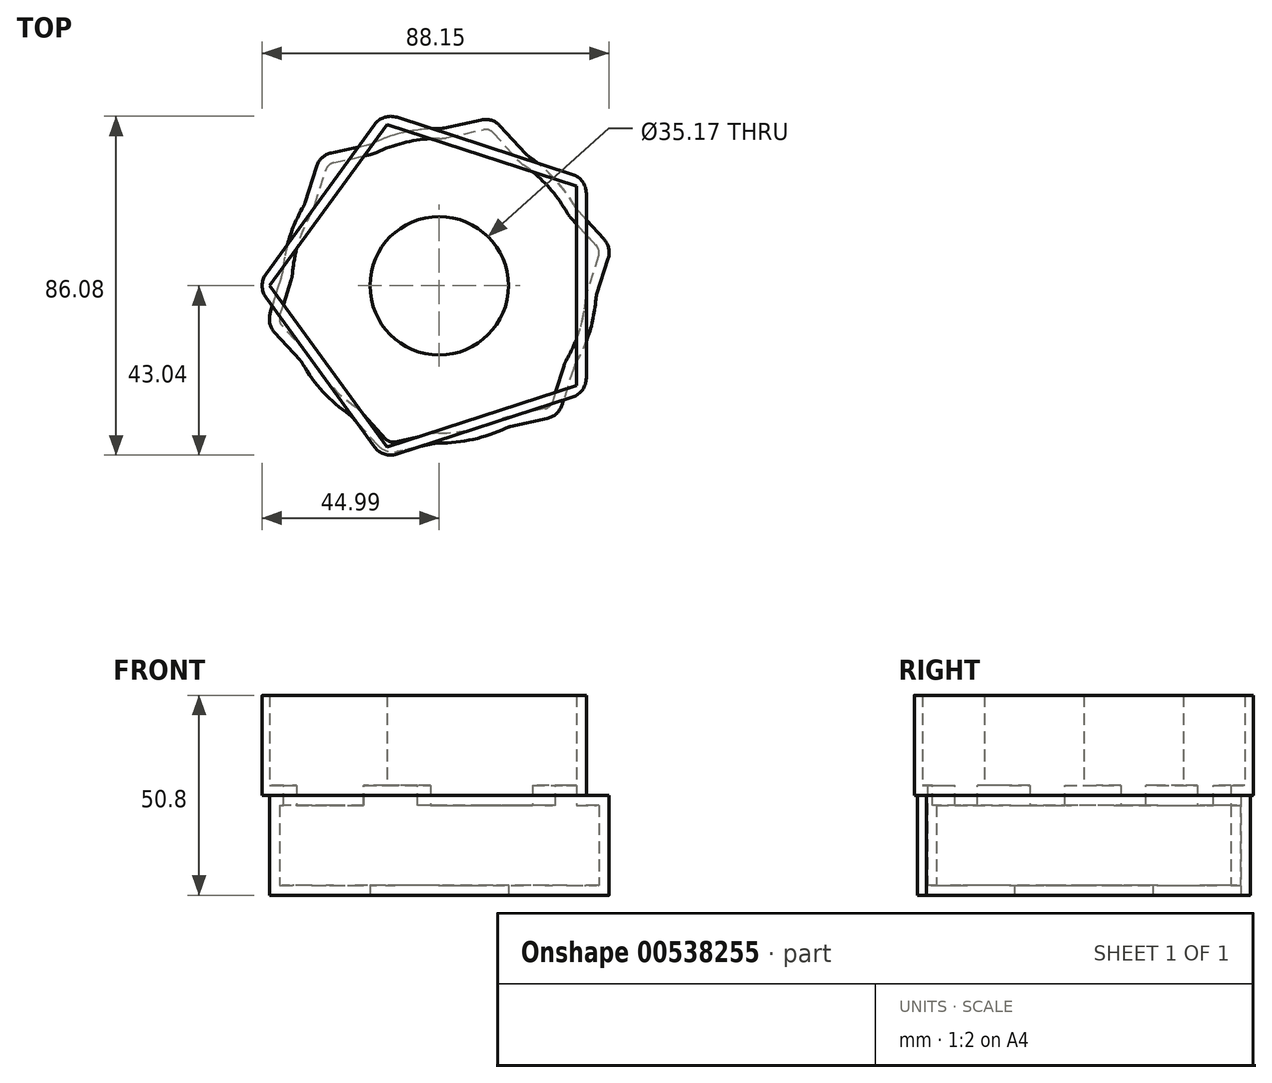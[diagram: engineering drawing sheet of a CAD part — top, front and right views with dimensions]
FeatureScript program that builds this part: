
annotation { "Feature Type Name" : "Feature", "Feature Type Description" : "" }
export const myFeature = defineFeature(function(context is Context, id is Id, definition is map)
    precondition{}
    {
        {
            var Q0;
            Q0=qCreatedBy(makeId("Top.planeOp"),FACE);
            var sketch = newSketch(context, id + "F0", { "sketchPlane" : qUnion([Q0])});
            skCircle(sketch, "E0", {"center": v(0, 0) * mm, "radius": 39.95 * mm});
            skSolve(sketch);
        }
        {
            var Q0;
            Q0 = qSketchRegion(id + "F0", true);
            extrude(context, id + "F1", {"entities" : qUnion([Q0]), "depth" : 25.4 * mm, "offsetDistance" : 25.4 * mm});
        }
        {
            var Q0;
            Q0=qCreatedBy(makeId("Top.planeOp"),FACE);
            var sketch = newSketch(context, id + "F2", { "sketchPlane" : qUnion([Q0])});
            skCircle(sketch, "E1.cCircle", {"center": v(0, 0) * mm, "radius": 44.86 * mm, "construction": true});
            skLineSegment(sketch, "E1.0", {"start": v(-43.8, -9.68) * mm, "end": v(-30.29, 33.1) * mm});
            skLineSegment(sketch, "E1.1", {"start": v(-30.29, 33.1) * mm, "end": v(13.52, 42.78) * mm});
            skLineSegment(sketch, "E1.2", {"start": v(13.52, 42.78) * mm, "end": v(43.8, 9.68) * mm});
            skLineSegment(sketch, "E1.3", {"start": v(43.8, 9.68) * mm, "end": v(30.29, -33.1) * mm});
            skLineSegment(sketch, "E1.4", {"start": v(30.29, -33.1) * mm, "end": v(-13.52, -42.78) * mm});
            skLineSegment(sketch, "E1.5", {"start": v(-13.52, -42.78) * mm, "end": v(-43.8, -9.68) * mm});
            skSolve(sketch);
        }
        {
            var Q0;
            Q0 = qSketchRegion(id + "F2", true);
            extrude(context, id + "F3", {"entities" : qUnion([Q0]), "operationType" : NewBodyOperationType.ADD, "depth" : 25.4 * mm, "offsetDistance" : 25.4 * mm});
        }
        {
            var Q0;
            Q0=makeQuery(id+"F3.opExtrude","SWEPT_EDGE",EDGE,{"disambiguationData":[OSD([sQuery(id+"F2.wireOp",EDGE,"E1.0"),sQuery(id+"F2.wireOp",EDGE,"E1.5")])]});
            var Q1;
            Q1=makeQuery(id+"F3.boolean.opBoolean","INTERSECT",EDGE,{"disambiguationData":[OD(0.0)],"derivedFrom":[makeQuery(id+"F1.opExtrude","SWEPT_FACE",FACE,{"disambiguationData":[OSD([sQuery(id+"F0.wireOp",EDGE,"E0")])]}),makeQuery(id+"F3.opExtrude","SWEPT_FACE",FACE,{"disambiguationData":[OSD([sQuery(id+"F2.wireOp",EDGE,"E1.0")])]})]});
            var Q2;
            Q2=makeQuery(id+"F3.boolean.opBoolean","INTERSECT",EDGE,{"disambiguationData":[OD(1.0)],"derivedFrom":[makeQuery(id+"F1.opExtrude","SWEPT_FACE",FACE,{"disambiguationData":[OSD([sQuery(id+"F0.wireOp",EDGE,"E0")])]}),makeQuery(id+"F3.opExtrude","SWEPT_FACE",FACE,{"disambiguationData":[OSD([sQuery(id+"F2.wireOp",EDGE,"E1.0")])]})]});
            var Q3;
            Q3=makeQuery(id+"F3.boolean.opBoolean","INTERSECT",EDGE,{"disambiguationData":[OD(0.0)],"derivedFrom":[makeQuery(id+"F1.opExtrude","SWEPT_FACE",FACE,{"disambiguationData":[OSD([sQuery(id+"F0.wireOp",EDGE,"E0")])]}),makeQuery(id+"F3.opExtrude","SWEPT_FACE",FACE,{"disambiguationData":[OSD([sQuery(id+"F2.wireOp",EDGE,"E1.5")])]})]});
            fillet(context, id + "F4", {"entities" : qUnion([Q0, Q1, Q2, Q3]), "radius" : 5.08 * mm, "tangentPropagation" : true, "allowEdgeOverflow" : false});
        }
        {
            var Q0;
            Q0=makeQuery(id+"F3.boolean.opBoolean","INTERSECT",EDGE,{"disambiguationData":[OD(1.0)],"derivedFrom":[makeQuery(id+"F1.opExtrude","SWEPT_FACE",FACE,{"disambiguationData":[OSD([sQuery(id+"F0.wireOp",EDGE,"E0")])]}),makeQuery(id+"F3.opExtrude","SWEPT_FACE",FACE,{"disambiguationData":[OSD([sQuery(id+"F2.wireOp",EDGE,"E1.5")])]})]});
            var Q1;
            Q1=makeQuery(id+"F3.opExtrude","SWEPT_EDGE",EDGE,{"disambiguationData":[OSD([sQuery(id+"F2.wireOp",EDGE,"E1.4"),sQuery(id+"F2.wireOp",EDGE,"E1.5")])]});
            var Q2;
            Q2=makeQuery(id+"F3.boolean.opBoolean","INTERSECT",EDGE,{"disambiguationData":[OD(1.0)],"derivedFrom":[makeQuery(id+"F1.opExtrude","SWEPT_FACE",FACE,{"disambiguationData":[OSD([sQuery(id+"F0.wireOp",EDGE,"E0")])]}),makeQuery(id+"F3.opExtrude","SWEPT_FACE",FACE,{"disambiguationData":[OSD([sQuery(id+"F2.wireOp",EDGE,"E1.4")])]})]});
            var Q3;
            Q3=makeQuery(id+"F3.boolean.opBoolean","INTERSECT",EDGE,{"disambiguationData":[OD(0.0)],"derivedFrom":[makeQuery(id+"F1.opExtrude","SWEPT_FACE",FACE,{"disambiguationData":[OSD([sQuery(id+"F0.wireOp",EDGE,"E0")])]}),makeQuery(id+"F3.opExtrude","SWEPT_FACE",FACE,{"disambiguationData":[OSD([sQuery(id+"F2.wireOp",EDGE,"E1.4")])]})]});
            var Q4;
            Q4=makeQuery(id+"F3.opExtrude","SWEPT_EDGE",EDGE,{"disambiguationData":[OSD([sQuery(id+"F2.wireOp",EDGE,"E1.3"),sQuery(id+"F2.wireOp",EDGE,"E1.4")])]});
            var Q5;
            Q5=makeQuery(id+"F3.boolean.opBoolean","INTERSECT",EDGE,{"disambiguationData":[OD(1.0)],"derivedFrom":[makeQuery(id+"F1.opExtrude","SWEPT_FACE",FACE,{"disambiguationData":[OSD([sQuery(id+"F0.wireOp",EDGE,"E0")])]}),makeQuery(id+"F3.opExtrude","SWEPT_FACE",FACE,{"disambiguationData":[OSD([sQuery(id+"F2.wireOp",EDGE,"E1.3")])]})]});
            var Q6;
            Q6=makeQuery(id+"F3.boolean.opBoolean","INTERSECT",EDGE,{"disambiguationData":[OD(0.0)],"derivedFrom":[makeQuery(id+"F1.opExtrude","SWEPT_FACE",FACE,{"disambiguationData":[OSD([sQuery(id+"F0.wireOp",EDGE,"E0")])]}),makeQuery(id+"F3.opExtrude","SWEPT_FACE",FACE,{"disambiguationData":[OSD([sQuery(id+"F2.wireOp",EDGE,"E1.3")])]})]});
            var Q7;
            Q7=makeQuery(id+"F3.opExtrude","SWEPT_EDGE",EDGE,{"disambiguationData":[OSD([sQuery(id+"F2.wireOp",EDGE,"E1.2"),sQuery(id+"F2.wireOp",EDGE,"E1.3")])]});
            var Q8;
            Q8=makeQuery(id+"F3.boolean.opBoolean","INTERSECT",EDGE,{"disambiguationData":[OD(1.0)],"derivedFrom":[makeQuery(id+"F1.opExtrude","SWEPT_FACE",FACE,{"disambiguationData":[OSD([sQuery(id+"F0.wireOp",EDGE,"E0")])]}),makeQuery(id+"F3.opExtrude","SWEPT_FACE",FACE,{"disambiguationData":[OSD([sQuery(id+"F2.wireOp",EDGE,"E1.2")])]})]});
            var Q9;
            Q9=makeQuery(id+"F3.boolean.opBoolean","INTERSECT",EDGE,{"disambiguationData":[OD(0.0)],"derivedFrom":[makeQuery(id+"F1.opExtrude","SWEPT_FACE",FACE,{"disambiguationData":[OSD([sQuery(id+"F0.wireOp",EDGE,"E0")])]}),makeQuery(id+"F3.opExtrude","SWEPT_FACE",FACE,{"disambiguationData":[OSD([sQuery(id+"F2.wireOp",EDGE,"E1.2")])]})]});
            var Q10;
            Q10=makeQuery(id+"F3.opExtrude","SWEPT_EDGE",EDGE,{"disambiguationData":[OSD([sQuery(id+"F2.wireOp",EDGE,"E1.1"),sQuery(id+"F2.wireOp",EDGE,"E1.2")])]});
            var Q11;
            Q11=makeQuery(id+"F3.boolean.opBoolean","INTERSECT",EDGE,{"disambiguationData":[OD(1.0)],"derivedFrom":[makeQuery(id+"F1.opExtrude","SWEPT_FACE",FACE,{"disambiguationData":[OSD([sQuery(id+"F0.wireOp",EDGE,"E0")])]}),makeQuery(id+"F3.opExtrude","SWEPT_FACE",FACE,{"disambiguationData":[OSD([sQuery(id+"F2.wireOp",EDGE,"E1.1")])]})]});
            var Q12;
            Q12=makeQuery(id+"F3.boolean.opBoolean","INTERSECT",EDGE,{"disambiguationData":[OD(0.0)],"derivedFrom":[makeQuery(id+"F1.opExtrude","SWEPT_FACE",FACE,{"disambiguationData":[OSD([sQuery(id+"F0.wireOp",EDGE,"E0")])]}),makeQuery(id+"F3.opExtrude","SWEPT_FACE",FACE,{"disambiguationData":[OSD([sQuery(id+"F2.wireOp",EDGE,"E1.1")])]})]});
            var Q13;
            Q13=makeQuery(id+"F3.opExtrude","SWEPT_EDGE",EDGE,{"disambiguationData":[OSD([sQuery(id+"F2.wireOp",EDGE,"E1.0"),sQuery(id+"F2.wireOp",EDGE,"E1.1")])]});
            var Q14;
            {var subQ4=sQuery(id+"F2.wireOp",EDGE,"E1.1");var subQ5=sQuery(id+"F2.wireOp",EDGE,"E1.0");var subQ6=sQuery(id+"F0.wireOp",EDGE,"E0");var subQ7=makeQuery(id+"F1.opExtrude","SWEPT_FACE",FACE,{"disambiguationData":[OSD([subQ6])]});var subQ8=makeQuery(id+"F3.opExtrude","SWEPT_FACE",FACE,{"disambiguationData":[OSD([subQ5])]});Q14=makeQuery(id+"F4.opFillet","BLEND_EDGE",EDGE,{"blendedFrom":[makeQuery(id+"F3.boolean.opBoolean","INTERSECT",EDGE,{"disambiguationData":[OD(1.0)],"derivedFrom":[subQ7,subQ8]}),makeQuery(id+"F3.boolean.opBoolean","SPLIT",FACE,{"disambiguationData":[TD([makeQuery(id+"F3.opExtrude","SWEPT_FACE",FACE,{"disambiguationData":[OSD([subQ4])]})])],"derivedFrom":subQ8})],"blendedInto":[makeQuery(id+"F3.boolean.opBoolean","SPLIT",FACE,{"disambiguationData":[TD([makeQuery(id+"F3.opExtrude","SWEPT_FACE",FACE,{"disambiguationData":[OSD([subQ4])]})])],"derivedFrom":subQ8})]});}
            var Q15;
            {var subQ0=sQuery(id+"F2.wireOp",EDGE,"E1.5");var subQ5=sQuery(id+"F2.wireOp",EDGE,"E1.0");var subQ6=sQuery(id+"F0.wireOp",EDGE,"E0");var subQ7=makeQuery(id+"F1.opExtrude","SWEPT_FACE",FACE,{"disambiguationData":[OSD([subQ6])]});var subQ8=makeQuery(id+"F3.opExtrude","SWEPT_FACE",FACE,{"disambiguationData":[OSD([subQ5])]});Q15=makeQuery(id+"F4.opFillet","BLEND_EDGE",EDGE,{"blendedFrom":[makeQuery(id+"F3.boolean.opBoolean","INTERSECT",EDGE,{"disambiguationData":[OD(0.0)],"derivedFrom":[subQ7,subQ8]}),makeQuery(id+"F3.boolean.opBoolean","SPLIT",FACE,{"disambiguationData":[TD([makeQuery(id+"F3.opExtrude","SWEPT_FACE",FACE,{"disambiguationData":[OSD([subQ0])]})])],"derivedFrom":subQ8})],"blendedInto":[makeQuery(id+"F3.boolean.opBoolean","SPLIT",FACE,{"disambiguationData":[TD([makeQuery(id+"F3.opExtrude","SWEPT_FACE",FACE,{"disambiguationData":[OSD([subQ0])]})])],"derivedFrom":subQ8})]});}
            var Q16;
            {var subQ0=sQuery(id+"F2.wireOp",EDGE,"E1.0");var subQ2=sQuery(id+"F2.wireOp",EDGE,"E1.5");Q16=makeQuery(id+"F4.opFillet","BLEND_EDGE",EDGE,{"blendedFrom":[makeQuery(id+"F3.opExtrude","SWEPT_EDGE",EDGE,{"disambiguationData":[OSD([subQ0,subQ2])]}),makeQuery(id+"F3.boolean.opBoolean","SPLIT",FACE,{"disambiguationData":[TD([makeQuery(id+"F3.opExtrude","SWEPT_FACE",FACE,{"disambiguationData":[OSD([subQ0])]})])],"derivedFrom":makeQuery(id+"F3.opExtrude","SWEPT_FACE",FACE,{"disambiguationData":[OSD([subQ2])]})})],"blendedInto":[makeQuery(id+"F3.boolean.opBoolean","SPLIT",FACE,{"disambiguationData":[TD([makeQuery(id+"F3.opExtrude","SWEPT_FACE",FACE,{"disambiguationData":[OSD([subQ0])]})])],"derivedFrom":makeQuery(id+"F3.opExtrude","SWEPT_FACE",FACE,{"disambiguationData":[OSD([subQ2])]})})]});}
            var Q17;
            {var subQ0=sQuery(id+"F2.wireOp",EDGE,"E1.5");var subQ5=sQuery(id+"F2.wireOp",EDGE,"E1.0");Q17=makeQuery(id+"F4.opFillet","BLEND_EDGE",EDGE,{"blendedFrom":[makeQuery(id+"F3.opExtrude","SWEPT_EDGE",EDGE,{"disambiguationData":[OSD([subQ5,subQ0])]}),makeQuery(id+"F3.boolean.opBoolean","SPLIT",FACE,{"disambiguationData":[TD([makeQuery(id+"F3.opExtrude","SWEPT_FACE",FACE,{"disambiguationData":[OSD([subQ0])]})])],"derivedFrom":makeQuery(id+"F3.opExtrude","SWEPT_FACE",FACE,{"disambiguationData":[OSD([subQ5])]})})],"blendedInto":[makeQuery(id+"F3.boolean.opBoolean","SPLIT",FACE,{"disambiguationData":[TD([makeQuery(id+"F3.opExtrude","SWEPT_FACE",FACE,{"disambiguationData":[OSD([subQ0])]})])],"derivedFrom":makeQuery(id+"F3.opExtrude","SWEPT_FACE",FACE,{"disambiguationData":[OSD([subQ5])]})})]});}
            fillet(context, id + "F5", {"entities" : qUnion([Q0, Q1, Q2, Q3, Q4, Q5, Q6, Q7, Q8, Q9, Q10, Q11, Q12, Q13, Q14, Q15, Q16, Q17]), "radius" : 5.08 * mm, "tangentPropagation" : true, "allowEdgeOverflow" : false});
        }
        {
            var Q0;
            Q0=makeQuery(id+"F3.boolean.opBoolean","MERGE",FACE,{"derivedFrom":[makeQuery(id+"F1.opExtrude","CAP_FACE",FACE,{"disambiguationData":[OSD([sQuery(id+"F0.wireOp",EDGE,"E0")])],"isStart":false}),makeQuery(id+"F3.opExtrude","CAP_FACE",FACE,{"disambiguationData":[OSD([sQuery(id+"F2.wireOp",EDGE,"E1.0"),sQuery(id+"F2.wireOp",EDGE,"E1.1"),sQuery(id+"F2.wireOp",EDGE,"E1.2"),sQuery(id+"F2.wireOp",EDGE,"E1.3"),sQuery(id+"F2.wireOp",EDGE,"E1.4"),sQuery(id+"F2.wireOp",EDGE,"E1.5")])],"isStart":false})]});
            var sketch = newSketch(context, id + "F6", { "sketchPlane" : qUnion([Q0])});
            skCircle(sketch, "E2.cCircle", {"center": v(0, 0) * mm, "radius": 46.19 * mm, "construction": true});
            skLineSegment(sketch, "E2.0", {"start": v(-46.19, 0) * mm, "end": v(-14.27, 43.93) * mm});
            skLineSegment(sketch, "E2.1", {"start": v(-14.27, 43.93) * mm, "end": v(37.37, 27.15) * mm});
            skLineSegment(sketch, "E2.2", {"start": v(37.37, 27.15) * mm, "end": v(37.37, -27.15) * mm});
            skLineSegment(sketch, "E2.3", {"start": v(37.37, -27.15) * mm, "end": v(-14.27, -43.93) * mm});
            skLineSegment(sketch, "E2.4", {"start": v(-14.27, -43.93) * mm, "end": v(-46.19, 0) * mm});
            skSolve(sketch);
        }
        {
            var Q0;
            Q0 = qSketchRegion(id + "F6", true);
            extrude(context, id + "F7", {"entities" : qUnion([Q0]), "operationType" : NewBodyOperationType.ADD, "depth" : 25.4 * mm, "offsetDistance" : 25.4 * mm});
        }
        {
            var Q0;
            Q0=makeQuery(id+"F7.opExtrude","CAP_FACE",FACE,{"disambiguationData":[OSD([sQuery(id+"F6.wireOp",EDGE,"E2.0"),sQuery(id+"F6.wireOp",EDGE,"E2.1"),sQuery(id+"F6.wireOp",EDGE,"E2.2"),sQuery(id+"F6.wireOp",EDGE,"E2.3"),sQuery(id+"F6.wireOp",EDGE,"E2.4")])],"isStart":false});
            shell(context, id + "F8", {"entities" : qUnion([Q0]), "thickness" : 2.54 * mm});
        }
        {
            var Q0;
            Q0=makeQuery(id+"F3.boolean.opBoolean","MERGE",FACE,{"derivedFrom":[makeQuery(id+"F1.opExtrude","CAP_FACE",FACE,{"disambiguationData":[OSD([sQuery(id+"F0.wireOp",EDGE,"E0")])],"isStart":true}),makeQuery(id+"F3.opExtrude","CAP_FACE",FACE,{"disambiguationData":[OSD([sQuery(id+"F2.wireOp",EDGE,"E1.0"),sQuery(id+"F2.wireOp",EDGE,"E1.1"),sQuery(id+"F2.wireOp",EDGE,"E1.2"),sQuery(id+"F2.wireOp",EDGE,"E1.3"),sQuery(id+"F2.wireOp",EDGE,"E1.4"),sQuery(id+"F2.wireOp",EDGE,"E1.5")])],"isStart":true})]});
            var sketch = newSketch(context, id + "F9", { "sketchPlane" : qUnion([Q0])});
            skCircle(sketch, "E3", {"center": v(0, 0) * mm, "radius": 17.59 * mm});
            skSolve(sketch);
        }
        {
            var Q0;
            Q0 = qSketchRegion(id + "F9", true);
            extrude(context, id + "F10", {"entities" : qUnion([Q0]), "operationType" : NewBodyOperationType.REMOVE, "oppositeDirection" : true, "depth" : 203.2 * mm, "offsetDistance" : 25.4 * mm});
        }
        {
            var Q0;
            Q0=makeQuery(id+"F7.opExtrude","SWEPT_EDGE",EDGE,{"disambiguationData":[OSD([sQuery(id+"F6.wireOp",EDGE,"E2.3"),sQuery(id+"F6.wireOp",EDGE,"E2.4")])]});
            var Q1;
            Q1=makeQuery(id+"F7.opExtrude","SWEPT_EDGE",EDGE,{"disambiguationData":[OSD([sQuery(id+"F6.wireOp",EDGE,"E2.0"),sQuery(id+"F6.wireOp",EDGE,"E2.4")])]});
            var Q2;
            Q2=makeQuery(id+"F7.opExtrude","SWEPT_EDGE",EDGE,{"disambiguationData":[OSD([sQuery(id+"F6.wireOp",EDGE,"E2.0"),sQuery(id+"F6.wireOp",EDGE,"E2.1")])]});
            var Q3;
            Q3=makeQuery(id+"F7.opExtrude","SWEPT_EDGE",EDGE,{"disambiguationData":[OSD([sQuery(id+"F6.wireOp",EDGE,"E2.1"),sQuery(id+"F6.wireOp",EDGE,"E2.2")])]});
            var Q4;
            Q4=makeQuery(id+"F7.opExtrude","SWEPT_EDGE",EDGE,{"disambiguationData":[OSD([sQuery(id+"F6.wireOp",EDGE,"E2.2"),sQuery(id+"F6.wireOp",EDGE,"E2.3")])]});
            fillet(context, id + "F11", {"entities" : qUnion([Q0, Q1, Q2, Q3, Q4]), "radius" : 5.08 * mm, "tangentPropagation" : true, "allowEdgeOverflow" : false});
        }
    });
